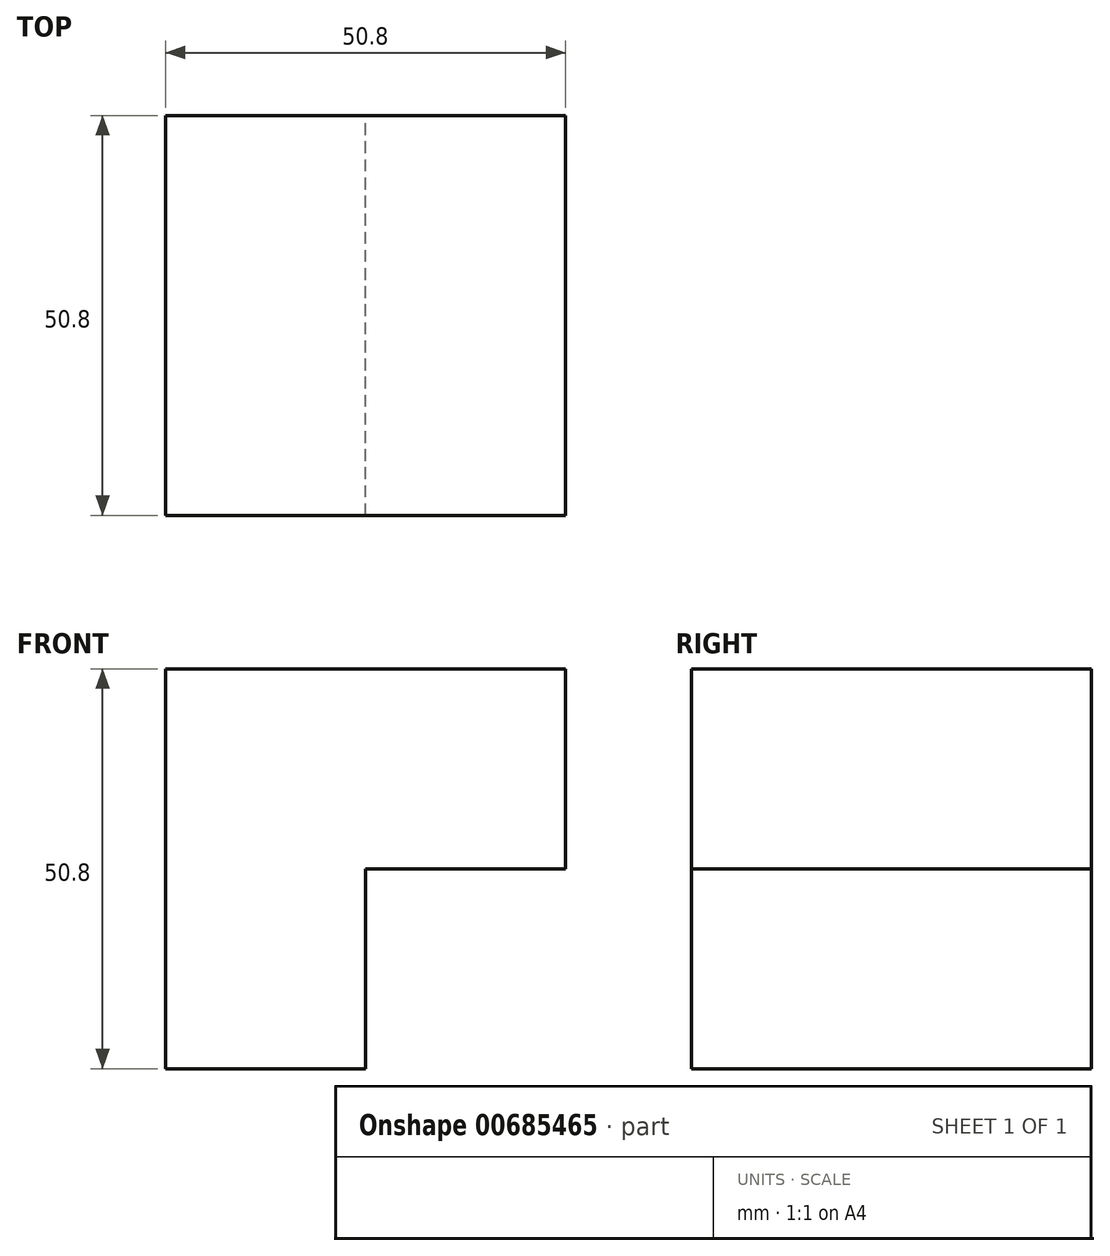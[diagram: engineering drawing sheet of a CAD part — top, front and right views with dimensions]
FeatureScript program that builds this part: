
annotation { "Feature Type Name" : "Feature", "Feature Type Description" : "" }
export const myFeature = defineFeature(function(context is Context, id is Id, definition is map)
    precondition{}
    {
        {
            var Q0;
            Q0=qCreatedBy(makeId("Front.planeOp"),FACE);
            var sketch = newSketch(context, id + "F0", { "sketchPlane" : qUnion([Q0])});
            skLineSegment(sketch, "E0", {"start": v(-43.06, 25.4) * mm, "end": v(-43.06, -25.4) * mm});
            skLineSegment(sketch, "E1", {"start": v(-43.06, -25.4) * mm, "end": v(-17.66, -25.4) * mm});
            skLineSegment(sketch, "E2", {"start": v(-17.66, -25.4) * mm, "end": v(-17.66, 0) * mm});
            skLineSegment(sketch, "E3", {"start": v(-17.66, 0) * mm, "end": v(7.74, 0) * mm});
            skLineSegment(sketch, "E4", {"start": v(7.74, 0) * mm, "end": v(7.74, 25.4) * mm});
            skLineSegment(sketch, "E5", {"start": v(7.74, 25.4) * mm, "end": v(-43.06, 25.4) * mm});
            skSolve(sketch);
        }
        {
            var Q0;
            Q0=makeQuery(id+"F0.imprint","IMPRINT",FACE,{"disambiguationData":[TD([[makeQuery(id+"F0.imprint","IMPRINT",EDGE,{"derivedFrom":sQuery(id+"F0.wireOp",EDGE,"E0")}),1.0]])]});
            extrude(context, id + "F1", {"entities" : qUnion([Q0]), "depth" : 50.8 * mm, "offsetDistance" : 25.4 * mm});
        }
    });
